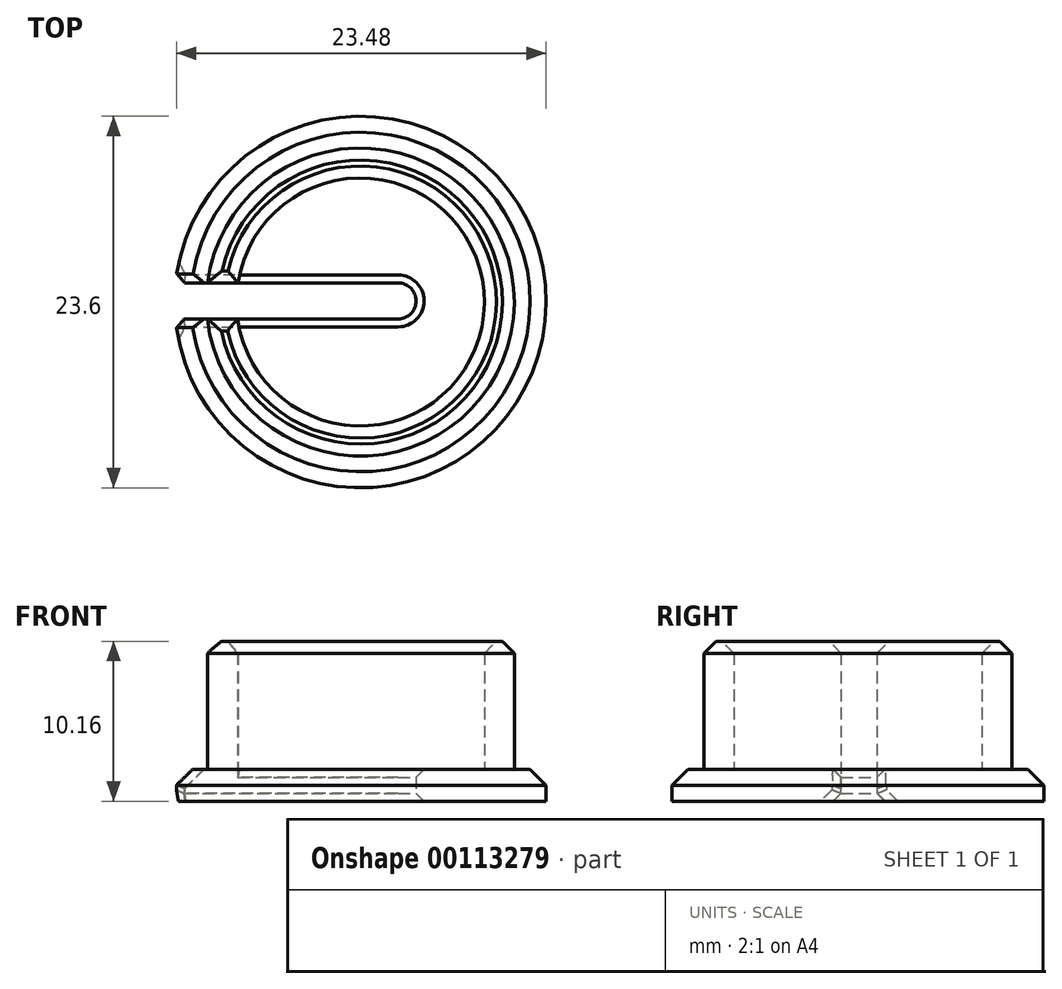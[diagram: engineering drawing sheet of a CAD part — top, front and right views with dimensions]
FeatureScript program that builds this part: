
annotation { "Feature Type Name" : "Feature", "Feature Type Description" : "" }
export const myFeature = defineFeature(function(context is Context, id is Id, definition is map)
    precondition{}
    {
        {
            var Q0;
            Q0=qCreatedBy(makeId("Top.planeOp"),FACE);
            var sketch = newSketch(context, id + "F0", { "sketchPlane" : qUnion([Q0])});
            skCircle(sketch, "E0", {"center": v(0, 0) * mm, "radius": 9.78 * mm});
            skCircle(sketch, "E1.0", {"center": v(0, 0) * mm, "radius": 7.87 * mm});
            skCircle(sketch, "E2", {"center": v(0, 0) * mm, "radius": 11.8 * mm});
            skLineSegment(sketch, "E3.bottom", {"start": v(-14.93, -1.07) * mm, "end": v(2.4, -1.07) * mm});
            skLineSegment(sketch, "E3.top", {"start": v(-14.93, 1.21) * mm, "end": v(2.4, 1.21) * mm});
            skLineSegment(sketch, "E3.left", {"start": v(-14.93, -1.07) * mm, "end": v(-14.93, 1.21) * mm});
            skLineSegment(sketch, "E3.right", {"start": v(2.4, -1.07) * mm, "end": v(2.4, 1.21) * mm});
            skArc(sketch, "E4", {"start": v(2.4, -1.07) * mm, "mid": v(3.54, 0.07) * mm, "end": v(2.4, 1.21) * mm});
            skSolve(sketch);
        }
        {
            var Q0;
            {var subQ0=sQuery(id+"F0.wireOp",EDGE,"E3.bottom");var subQ1=sQuery(id+"F0.wireOp",EDGE,"E0");var subQ2=makeQuery(id+"F0.imprint","INTERSECT",VERTEX,{"derivedFrom":[subQ1,subQ0]});Q0=makeQuery(id+"F0.imprint","IMPRINT",FACE,{"disambiguationData":[TD([[makeQuery(id+"F0.imprint","IMPRINT",EDGE,{"disambiguationData":[TD([[subQ2,-1.0]])],"derivedFrom":subQ1}),-1.0]])]});}
            var Q1;
            {var subQ0=sQuery(id+"F0.wireOp",EDGE,"E3.bottom");var subQ1=sQuery(id+"F0.wireOp",EDGE,"E0");var subQ2=makeQuery(id+"F0.imprint","INTERSECT",VERTEX,{"derivedFrom":[subQ1,subQ0]});Q1=makeQuery(id+"F0.imprint","IMPRINT",FACE,{"disambiguationData":[TD([[makeQuery(id+"F0.imprint","IMPRINT",EDGE,{"disambiguationData":[TD([[subQ2,1.0]])],"derivedFrom":subQ1}),-1.0]])]});}
            extrude(context, id + "F1", {"entities" : qUnion([Q0, Q1]), "depth" : 1.78 * mm});
        }
        {
            var Q0;
            Q0=sQuery(id+"F0.wireOp",EDGE,"E1.0");
            var Q1;
            Q1=sQuery(id+"F0.wireOp",EDGE,"E0");
            extrude(context, id + "F2", {"bodyType" : ToolBodyType.SURFACE, "surfaceEntities" : qUnion([Q0, Q1]), "depth" : 10.16 * mm});
        }
        {
            var Q0;
            Q0=makeQuery(id+"F2.opExtrude","SWEPT_BODY",BODY,{"disambiguationData":[OSD([sQuery(id+"F0.wireOp",EDGE,"E0")])]});
            deleteBodies(context, id + "F3", {"entities" : qUnion([Q0])});
        }
        {
            var Q0;
            Q0=makeQuery(id+"F2.opExtrude","SWEPT_BODY",BODY,{"disambiguationData":[OSD([sQuery(id+"F0.wireOp",EDGE,"E1.0")])]});
            deleteBodies(context, id + "F4", {"entities" : qUnion([Q0])});
        }
        {
            var Q0;
            Q0=makeQuery(id+"F1.opExtrude","SWEPT_BODY",BODY,{"disambiguationData":[OSD([sQuery(id+"F0.wireOp",EDGE,"E0"),sQuery(id+"F0.wireOp",EDGE,"E2")])]});
            deleteBodies(context, id + "F5", {"entities" : qUnion([Q0])});
        }
        {
            var Q0;
            {var subQ0=sQuery(id+"F0.wireOp",EDGE,"E3.bottom");var subQ1=sQuery(id+"F0.wireOp",EDGE,"E0");var subQ2=makeQuery(id+"F0.imprint","INTERSECT",VERTEX,{"derivedFrom":[subQ1,subQ0]});Q0=makeQuery(id+"F0.imprint","IMPRINT",FACE,{"disambiguationData":[TD([[makeQuery(id+"F0.imprint","IMPRINT",EDGE,{"disambiguationData":[TD([[subQ2,-1.0]])],"derivedFrom":subQ1}),-1.0]])]});}
            var Q1;
            {var subQ0=sQuery(id+"F0.wireOp",EDGE,"E3.bottom");var subQ1=sQuery(id+"F0.wireOp",EDGE,"E0");var subQ2=makeQuery(id+"F0.imprint","INTERSECT",VERTEX,{"derivedFrom":[subQ1,subQ0]});Q1=makeQuery(id+"F0.imprint","IMPRINT",FACE,{"disambiguationData":[TD([[makeQuery(id+"F0.imprint","IMPRINT",EDGE,{"disambiguationData":[TD([[subQ2,-1.0]])],"derivedFrom":subQ1}),1.0]])]});}
            var Q2;
            {var subQ5=sQuery(id+"F0.wireOp",EDGE,"E4");Q2=makeQuery(id+"F0.imprint","IMPRINT",FACE,{"disambiguationData":[TD([[makeQuery(id+"F0.imprint","IMPRINT",EDGE,{"derivedFrom":subQ5}),-1.0]])]});}
            extrude(context, id + "F6", {"entities" : qUnion([Q0, Q1, Q2]), "depth" : 2.03 * mm});
        }
        {
            var Q0;
            {var subQ0=sQuery(id+"F0.wireOp",EDGE,"E3.bottom");var subQ1=sQuery(id+"F0.wireOp",EDGE,"E0");var subQ2=makeQuery(id+"F0.imprint","INTERSECT",VERTEX,{"derivedFrom":[subQ1,subQ0]});Q0=makeQuery(id+"F0.imprint","IMPRINT",FACE,{"disambiguationData":[TD([[makeQuery(id+"F0.imprint","IMPRINT",EDGE,{"disambiguationData":[TD([[subQ2,-1.0]])],"derivedFrom":subQ1}),1.0]])]});}
            extrude(context, id + "F7", {"entities" : qUnion([Q0]), "operationType" : NewBodyOperationType.ADD, "depth" : 10.16 * mm});
        }
        {
            var Q0;
            Q0=makeQuery(id+"F7.opExtrude","CAP_FACE",FACE,{"disambiguationData":[OSD([sQuery(id+"F0.wireOp",EDGE,"E0"),sQuery(id+"F0.wireOp",EDGE,"E1.0"),sQuery(id+"F0.wireOp",EDGE,"E3.bottom"),sQuery(id+"F0.wireOp",EDGE,"E3.top")])],"isStart":false});
            chamfer(context, id + "F8", {"entities" : qUnion([Q0]), "width" : 0.76 * mm, "tangentPropagation" : true});
        }
        {
            var Q0;
            Q0=makeQuery(id+"F6.opExtrude","CAP_EDGE",EDGE,{"disambiguationData":[OSD([sQuery(id+"F0.wireOp",EDGE,"E2")])],"isStart":false});
            chamfer(context, id + "F9", {"entities" : qUnion([Q0]), "width" : 1.02 * mm, "tangentPropagation" : true});
        }
        {
            var Q0;
            {var subQ0=sQuery(id+"F0.wireOp",EDGE,"E4");var subQ1=sQuery(id+"F0.wireOp",EDGE,"E3.bottom");Q0=makeQuery(id+"F7.boolean.opBoolean","SPLIT",EDGE,{"disambiguationData":[TD([makeQuery(id+"F6.opExtrude","SWEPT_FACE",FACE,{"disambiguationData":[OSD([subQ0])]})])],"derivedFrom":makeQuery(id+"F6.opExtrude","CAP_EDGE",EDGE,{"disambiguationData":[OSD([subQ1])],"isStart":false})});}
            var Q1;
            Q1=makeQuery(id+"F6.opExtrude","CAP_EDGE",EDGE,{"disambiguationData":[OSD([sQuery(id+"F0.wireOp",EDGE,"E4")])],"isStart":false});
            var Q2;
            {var subQ0=sQuery(id+"F0.wireOp",EDGE,"E4");var subQ1=sQuery(id+"F0.wireOp",EDGE,"E3.top");Q2=makeQuery(id+"F7.boolean.opBoolean","SPLIT",EDGE,{"disambiguationData":[TD([makeQuery(id+"F6.opExtrude","SWEPT_FACE",FACE,{"disambiguationData":[OSD([subQ0])]})])],"derivedFrom":makeQuery(id+"F6.opExtrude","CAP_EDGE",EDGE,{"disambiguationData":[OSD([subQ1])],"isStart":false})});}
            chamfer(context, id + "F10", {"entities" : qUnion([Q0, Q1, Q2]), "width" : 0.5 * mm, "tangentPropagation" : true});
        }
        {
            var Q0;
            Q0=makeQuery(id+"F6.opExtrude","CAP_EDGE",EDGE,{"disambiguationData":[OSD([sQuery(id+"F0.wireOp",EDGE,"E3.bottom")])],"isStart":true});
            var Q1;
            Q1=makeQuery(id+"F6.opExtrude","CAP_EDGE",EDGE,{"disambiguationData":[OSD([sQuery(id+"F0.wireOp",EDGE,"E3.top")])],"isStart":true});
            chamfer(context, id + "F11", {"entities" : qUnion([Q0, Q1]), "width" : 0.5 * mm, "tangentPropagation" : true});
        }
        {
            var Q0;
            Q0=makeQuery(id+"F6.opExtrude","SWEPT_EDGE",EDGE,{"disambiguationData":[OSD([sQuery(id+"F0.wireOp",EDGE,"E2"),sQuery(id+"F0.wireOp",EDGE,"E3.top")])]});
            var Q1;
            {var subQ0=sQuery(id+"F0.wireOp",EDGE,"E3.top");Q1=makeQuery(id+"F9.opChamfer","BLEND_EDGE",EDGE,{"blendedFrom":[makeQuery(id+"F6.opExtrude","CAP_EDGE",EDGE,{"disambiguationData":[OSD([sQuery(id+"F0.wireOp",EDGE,"E2")])],"isStart":false}),makeQuery(id+"F7.boolean.opBoolean","MERGE",FACE,{"derivedFrom":[makeQuery(id+"F6.opExtrude","SWEPT_FACE",FACE,{"disambiguationData":[OSD([subQ0])]}),makeQuery(id+"F7.opExtrude","SWEPT_FACE",FACE,{"disambiguationData":[OSD([subQ0])]})]})],"blendedInto":[makeQuery(id+"F7.boolean.opBoolean","MERGE",FACE,{"derivedFrom":[makeQuery(id+"F6.opExtrude","SWEPT_FACE",FACE,{"disambiguationData":[OSD([subQ0])]}),makeQuery(id+"F7.opExtrude","SWEPT_FACE",FACE,{"disambiguationData":[OSD([subQ0])]})]})]});}
            var Q2;
            Q2=makeQuery(id+"F11.opChamfer","BLEND_EDGE",EDGE,{"blendedFrom":[makeQuery(id+"F6.opExtrude","CAP_EDGE",EDGE,{"disambiguationData":[OSD([sQuery(id+"F0.wireOp",EDGE,"E3.top")])],"isStart":true}),makeQuery(id+"F6.opExtrude","SWEPT_FACE",FACE,{"disambiguationData":[OSD([sQuery(id+"F0.wireOp",EDGE,"E2")])]})],"blendedInto":[makeQuery(id+"F6.opExtrude","SWEPT_FACE",FACE,{"disambiguationData":[OSD([sQuery(id+"F0.wireOp",EDGE,"E2")])]})]});
            var Q3;
            Q3=makeQuery(id+"F11.opChamfer","BLEND_EDGE",EDGE,{"blendedFrom":[makeQuery(id+"F6.opExtrude","CAP_EDGE",EDGE,{"disambiguationData":[OSD([sQuery(id+"F0.wireOp",EDGE,"E3.bottom")])],"isStart":true}),makeQuery(id+"F6.opExtrude","SWEPT_FACE",FACE,{"disambiguationData":[OSD([sQuery(id+"F0.wireOp",EDGE,"E2")])]})],"blendedInto":[makeQuery(id+"F6.opExtrude","SWEPT_FACE",FACE,{"disambiguationData":[OSD([sQuery(id+"F0.wireOp",EDGE,"E2")])]})]});
            var Q4;
            Q4=makeQuery(id+"F6.opExtrude","SWEPT_EDGE",EDGE,{"disambiguationData":[OSD([sQuery(id+"F0.wireOp",EDGE,"E2"),sQuery(id+"F0.wireOp",EDGE,"E3.bottom")])]});
            var Q5;
            {var subQ0=sQuery(id+"F0.wireOp",EDGE,"E3.bottom");Q5=makeQuery(id+"F9.opChamfer","BLEND_EDGE",EDGE,{"blendedFrom":[makeQuery(id+"F6.opExtrude","CAP_EDGE",EDGE,{"disambiguationData":[OSD([sQuery(id+"F0.wireOp",EDGE,"E2")])],"isStart":false}),makeQuery(id+"F7.boolean.opBoolean","MERGE",FACE,{"derivedFrom":[makeQuery(id+"F6.opExtrude","SWEPT_FACE",FACE,{"disambiguationData":[OSD([subQ0])]}),makeQuery(id+"F7.opExtrude","SWEPT_FACE",FACE,{"disambiguationData":[OSD([subQ0])]})]})],"blendedInto":[makeQuery(id+"F7.boolean.opBoolean","MERGE",FACE,{"derivedFrom":[makeQuery(id+"F6.opExtrude","SWEPT_FACE",FACE,{"disambiguationData":[OSD([subQ0])]}),makeQuery(id+"F7.opExtrude","SWEPT_FACE",FACE,{"disambiguationData":[OSD([subQ0])]})]})]});}
            chamfer(context, id + "F12", {"entities" : qUnion([Q0, Q1, Q2, Q3, Q4, Q5]), "width" : 0.5 * mm, "tangentPropagation" : true});
        }
    });
